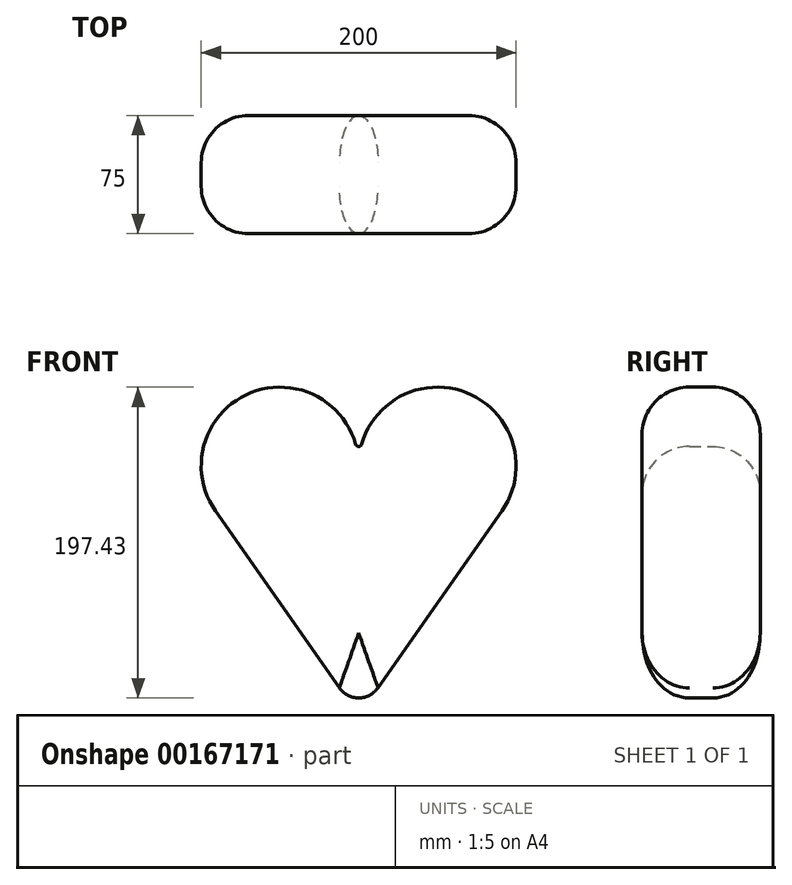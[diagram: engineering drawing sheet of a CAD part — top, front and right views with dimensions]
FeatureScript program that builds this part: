
annotation { "Feature Type Name" : "Feature", "Feature Type Description" : "" }
export const myFeature = defineFeature(function(context is Context, id is Id, definition is map)
    precondition{}
    {
        {
            var Q0;
            Q0=qCreatedBy(makeId("Front.planeOp"),FACE);
            var sketch = newSketch(context, id + "F0", { "sketchPlane" : qUnion([Q0])});
            skLineSegment(sketch, "E0", {"start": v(0, 0) * mm, "end": v(90.96, 129.9) * mm});
            skLineSegment(sketch, "E1", {"start": v(0, 0) * mm, "end": v(-90.96, 129.9) * mm});
            skLineSegment(sketch, "E2", {"start": v(0, 0) * mm, "end": v(0, 210.84) * mm, "construction": true});
            skArc(sketch, "E3", {"start": v(90.96, 129.9) * mm, "mid": v(71.5, 203.72) * mm, "end": v(1.92, 172.31) * mm});
            skArc(sketch, "E4", {"start": v(-1.92, 172.31) * mm, "mid": v(-71.5, 203.72) * mm, "end": v(-90.96, 129.9) * mm});
            skPoint(sketch, "E5.visualSharp", {"position": v(0, 158.58) * mm});
            skArc(sketch, "E5.filletArc", {"start": v(-1.92, 172.31) * mm, "mid": v(0, 170.86) * mm, "end": v(1.92, 172.31) * mm});
            skSolve(sketch);
        }
        {
            var Q0;
            Q0 = qSketchRegion(id + "F0", true);
            extrude(context, id + "F1", {"entities" : qUnion([Q0]), "depth" : 75 * mm});
        }
        {
            var Q0;
            Q0=makeQuery(id+"F1.opExtrude","SWEPT_EDGE",EDGE,{"disambiguationData":[OSD([sQuery(id+"F0.wireOp",EDGE,"E0"),sQuery(id+"F0.wireOp",EDGE,"E1")])]});
            fillet(context, id + "F2", {"entities" : qUnion([Q0]), "radius" : 15 * mm, "tangentPropagation" : true, "allowEdgeOverflow" : false});
        }
        {
            var Q0;
            Q0=makeQuery(id+"F1.opExtrude","CAP_EDGE",EDGE,{"disambiguationData":[OSD([sQuery(id+"F0.wireOp",EDGE,"E3")])],"isStart":false});
            var Q1;
            Q1=makeQuery(id+"F1.opExtrude","CAP_EDGE",EDGE,{"disambiguationData":[OSD([sQuery(id+"F0.wireOp",EDGE,"E3")])],"isStart":true});
            fillet(context, id + "F3", {"entities" : qUnion([Q0, Q1]), "radius" : 30 * mm, "tangentPropagation" : true, "allowEdgeOverflow" : false});
        }
    });
